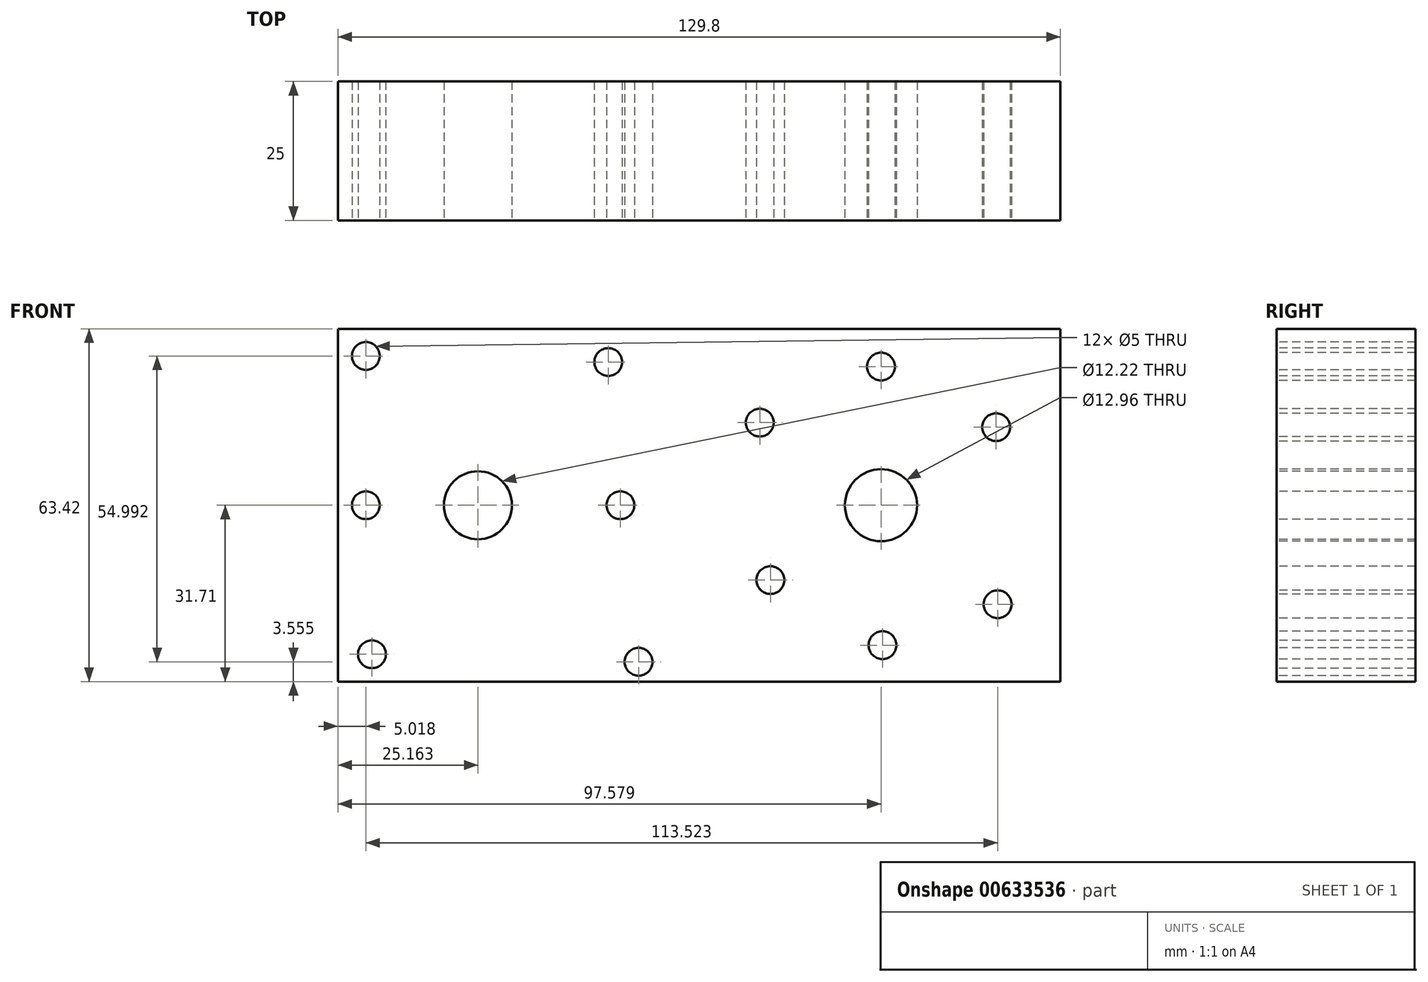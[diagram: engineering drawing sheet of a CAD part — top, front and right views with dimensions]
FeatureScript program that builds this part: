
annotation { "Feature Type Name" : "Feature", "Feature Type Description" : "" }
export const myFeature = defineFeature(function(context is Context, id is Id, definition is map)
    precondition{}
    {
        {
            var Q0;
            Q0=qCreatedBy(makeId("Front.planeOp"),FACE);
            var sketch = newSketch(context, id + "F0", { "sketchPlane" : qUnion([Q0])});
            skLineSegment(sketch, "E0.bottom", {"start": v(64.9, 31.7) * mm, "end": v(-64.9, 31.7) * mm});
            skLineSegment(sketch, "E0.top", {"start": v(64.9, -31.7) * mm, "end": v(-64.9, -31.7) * mm});
            skLineSegment(sketch, "E0.left", {"start": v(64.9, 31.7) * mm, "end": v(64.9, -31.7) * mm});
            skLineSegment(sketch, "E0.right", {"start": v(-64.9, 31.7) * mm, "end": v(-64.9, -31.7) * mm});
            skPoint(sketch, "E0.middle", {"position": v(0, 0) * mm});
            skSolve(sketch);
        }
        {
            var Q0;
            Q0 = qSketchRegion(id + "F0", true);
            extrude(context, id + "F1", {"entities" : qUnion([Q0]), "depth" : 25 * mm, "offsetDistance" : 25 * mm});
        }
        {
            var Q0;
            Q0=makeQuery(id+"F1.opExtrude","CAP_FACE",FACE,{"disambiguationData":[OSD([sQuery(id+"F0.wireOp",EDGE,"E0.bottom"),sQuery(id+"F0.wireOp",EDGE,"E0.top"),sQuery(id+"F0.wireOp",EDGE,"E0.left"),sQuery(id+"F0.wireOp",EDGE,"E0.right")])],"isStart":false});
            var sketch = newSketch(context, id + "F2", { "sketchPlane" : qUnion([Q0])});
            skCircle(sketch, "E1", {"center": v(-59.88, 26.84) * mm, "radius": 2.5 * mm});
            skCircle(sketch, "E2", {"center": v(-59.88, 0) * mm, "radius": 2.5 * mm});
            skCircle(sketch, "E3", {"center": v(-58.8, -26.8) * mm, "radius": 2.5 * mm});
            skCircle(sketch, "E4", {"center": v(-39.74, 0) * mm, "radius": 6.11 * mm});
            skCircle(sketch, "E5", {"center": v(-16.32, 25.75) * mm, "radius": 2.5 * mm});
            skCircle(sketch, "E6", {"center": v(-14.15, 0) * mm, "radius": 2.5 * mm});
            skCircle(sketch, "E7", {"center": v(-10.88, -28.16) * mm, "radius": 2.5 * mm});
            skCircle(sketch, "E8", {"center": v(10.9, 14.86) * mm, "radius": 2.5 * mm});
            skCircle(sketch, "E9", {"center": v(12.8, -13.45) * mm, "radius": 2.5 * mm});
            skCircle(sketch, "E10", {"center": v(32.68, 0) * mm, "radius": 6.48 * mm});
            skCircle(sketch, "E11", {"center": v(32.68, 24.93) * mm, "radius": 2.5 * mm});
            skCircle(sketch, "E12", {"center": v(32.95, -25.16) * mm, "radius": 2.5 * mm});
            skCircle(sketch, "E13", {"center": v(53.37, 14.04) * mm, "radius": 2.5 * mm});
            skCircle(sketch, "E14", {"center": v(53.64, -17.81) * mm, "radius": 2.5 * mm});
            skSolve(sketch);
        }
        {
            var Q0;
            Q0 = qSketchRegion(id + "F2", true);
            extrude(context, id + "F3", {"entities" : qUnion([Q0]), "operationType" : NewBodyOperationType.REMOVE, "oppositeDirection" : true, "depth" : 25 * mm, "offsetDistance" : 25 * mm});
        }
    });
